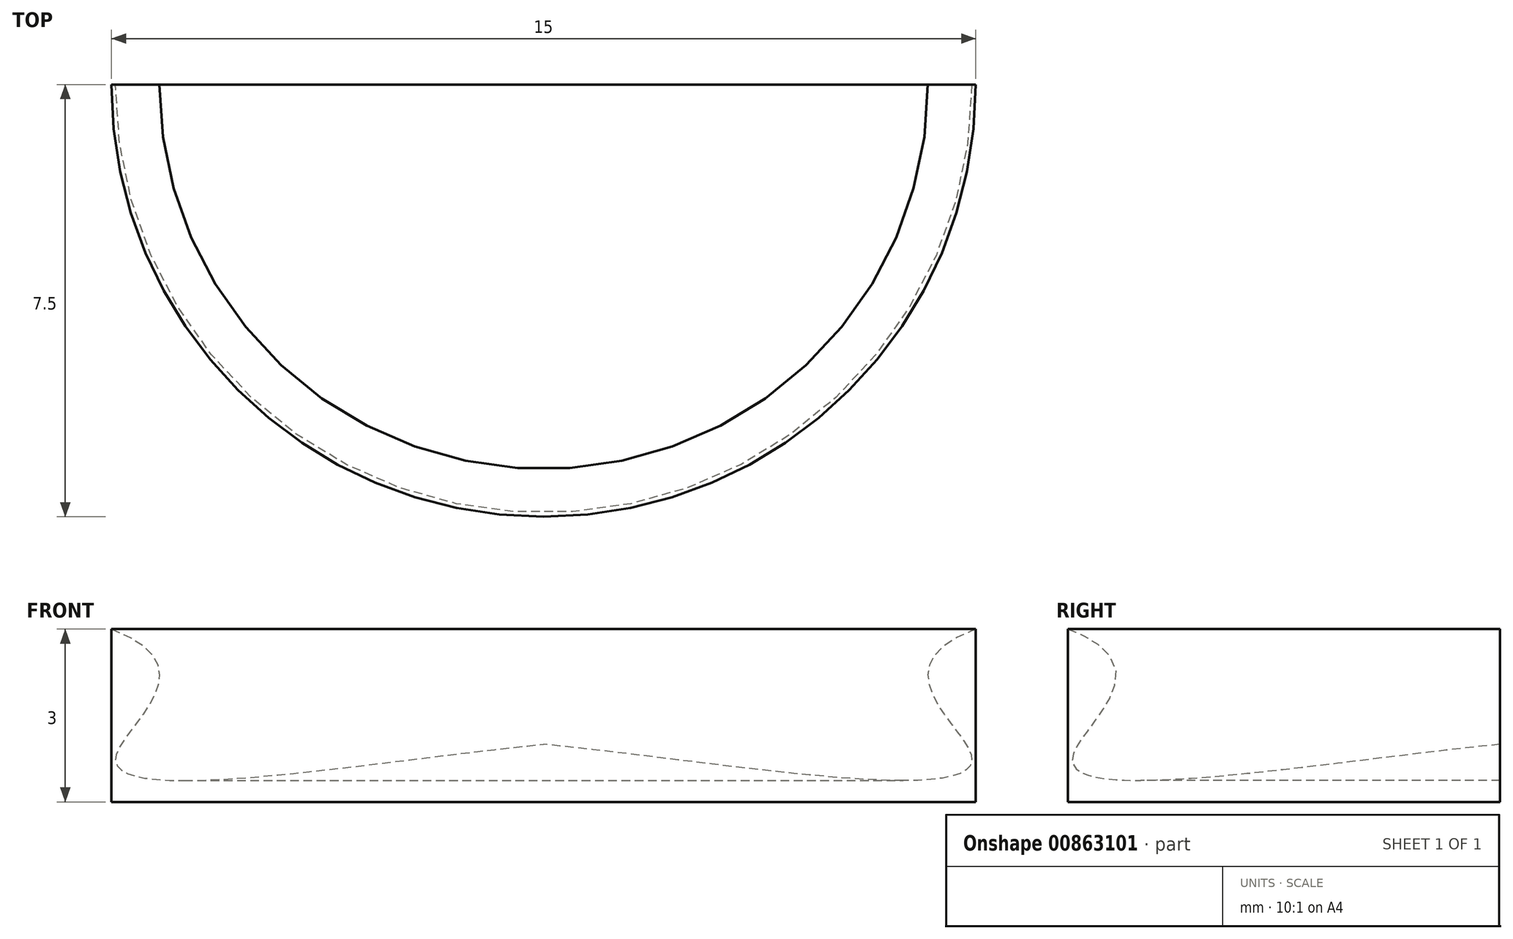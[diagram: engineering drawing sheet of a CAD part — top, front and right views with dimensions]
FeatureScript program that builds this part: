
annotation { "Feature Type Name" : "Feature", "Feature Type Description" : "" }
export const myFeature = defineFeature(function(context is Context, id is Id, definition is map)
    precondition{}
    {
        {
            var Q0;
            Q0=qCreatedBy(makeId("Top.planeOp"),FACE);
            var sketch = newSketch(context, id + "F0", { "sketchPlane" : qUnion([Q0])});
            skCircle(sketch, "E0", {"center": v(0, 0) * mm, "radius": 7.5 * mm});
            skSolve(sketch);
        }
        {
            var Q0;
            Q0=qCreatedBy(makeId("Front.planeOp"),FACE);
            var sketch = newSketch(context, id + "F1", { "sketchPlane" : qUnion([Q0])});
            skLineSegment(sketch, "E1", {"start": v(-7.5, 0) * mm, "end": v(-7.5, 3) * mm});
            skLineSegment(sketch, "E2", {"start": v(-7.5, 0) * mm, "end": v(0, 0) * mm});
            skLineSegment(sketch, "E3", {"start": v(0, 0) * mm, "end": v(0, 1) * mm});
            skFitSpline(sketch, "E4", {"points": [v(-7.5, 3) * mm, v(-7.42, 0.82) * mm, v(0, 1) * mm], "startDerivative": vector(14.9, -5.49) * mm, "endDerivative": vector(15.1, 1.52) * mm});
            skSolve(sketch);
        }
        {
            var Q0;
            Q0=qCreatedBy(makeId("Front.planeOp"),FACE);
            var sketch = newSketch(context, id + "F2", { "sketchPlane" : qUnion([Q0])});
            skLineSegment(sketch, "E5", {"start": v(0, 0) * mm, "end": v(0, 36.63) * mm, "construction": true});
            skSolve(sketch);
        }
        {
            var Q0;
            Q0=makeQuery(id+"F1.imprint","IMPRINT",FACE,{"disambiguationData":[TD([[makeQuery(id+"F1.imprint","IMPRINT",EDGE,{"derivedFrom":sQuery(id+"F1.wireOp",EDGE,"E1")}),-1.0]])]});
            var Q1;
            Q1=sQuery(id+"F2.wireOp",EDGE,"E5");
            revolve(context, id + "F3", {"surfaceOperationType" : NewSurfaceOperationType.NEW, "entities" : qUnion([Q0]), "axis" : qUnion([Q1]), "revolveType" : RevolveType.ONE_DIRECTION, "angle" : 180 * degree});
        }
    });
